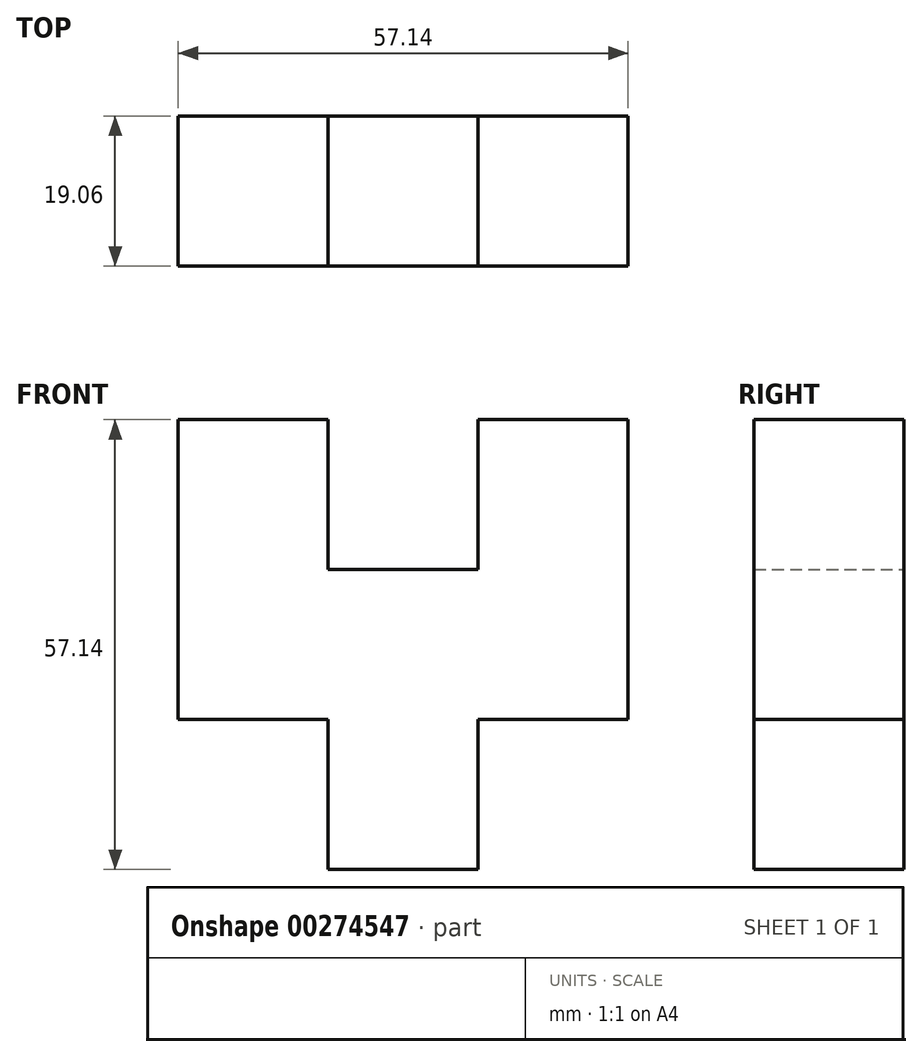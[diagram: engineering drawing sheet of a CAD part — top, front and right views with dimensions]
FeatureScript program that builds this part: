
annotation { "Feature Type Name" : "Feature", "Feature Type Description" : "" }
export const myFeature = defineFeature(function(context is Context, id is Id, definition is map)
    precondition{}
    {
        {
            var Q0;
            Q0=qCreatedBy(makeId("Front.planeOp"),FACE);
            var sketch = newSketch(context, id + "F0", { "sketchPlane" : qUnion([Q0])});
            skLineSegment(sketch, "E0.bottom", {"start": v(-9.53, 9.53) * mm, "end": v(9.53, 9.53) * mm});
            skLineSegment(sketch, "E0.top", {"start": v(-9.53, -9.53) * mm, "end": v(9.53, -9.53) * mm});
            skLineSegment(sketch, "E0.left", {"start": v(-9.53, 9.53) * mm, "end": v(-9.53, -9.53) * mm});
            skLineSegment(sketch, "E0.right", {"start": v(9.53, 9.53) * mm, "end": v(9.53, -9.53) * mm});
            skPoint(sketch, "E0.middle", {"position": v(0, 0) * mm});
            skLineSegment(sketch, "E1.top", {"start": v(9.53, -9.53) * mm, "end": v(28.58, -9.53) * mm});
            skLineSegment(sketch, "E1.right", {"start": v(28.58, 9.53) * mm, "end": v(28.58, -9.53) * mm});
            skPoint(sketch, "E1.middle", {"position": v(19.05, 0) * mm});
            skLineSegment(sketch, "E2.bottom", {"start": v(-28.58, 9.52) * mm, "end": v(-9.53, 9.52) * mm});
            skLineSegment(sketch, "E2.top", {"start": v(-28.58, -9.53) * mm, "end": v(-9.53, -9.53) * mm});
            skLineSegment(sketch, "E2.left", {"start": v(-28.58, 9.52) * mm, "end": v(-28.58, -9.53) * mm});
            skLineSegment(sketch, "E2.right", {"start": v(-9.53, 9.52) * mm, "end": v(-9.53, -9.53) * mm});
            skPoint(sketch, "E2.middle", {"position": v(-19.05, 0) * mm});
            skLineSegment(sketch, "E3.bottom", {"start": v(-28.58, 28.58) * mm, "end": v(-9.53, 28.58) * mm});
            skLineSegment(sketch, "E3.left", {"start": v(-28.58, 28.58) * mm, "end": v(-28.58, 9.52) * mm});
            skLineSegment(sketch, "E3.right", {"start": v(-9.53, 28.58) * mm, "end": v(-9.53, 9.52) * mm});
            skPoint(sketch, "E3.middle", {"position": v(-19.05, 19.05) * mm});
            skLineSegment(sketch, "E4.bottom", {"start": v(9.53, 28.57) * mm, "end": v(28.58, 28.57) * mm});
            skLineSegment(sketch, "E4.top", {"start": v(9.53, 9.52) * mm, "end": v(28.58, 9.52) * mm});
            skLineSegment(sketch, "E4.left", {"start": v(9.53, 28.57) * mm, "end": v(9.53, 9.52) * mm});
            skLineSegment(sketch, "E4.right", {"start": v(28.58, 28.57) * mm, "end": v(28.58, 9.52) * mm});
            skPoint(sketch, "E4.middle", {"position": v(19.05, 19.05) * mm});
            skLineSegment(sketch, "E5.bottom", {"start": v(-9.53, -9.53) * mm, "end": v(9.52, -9.53) * mm});
            skLineSegment(sketch, "E5.top", {"start": v(-9.53, -28.58) * mm, "end": v(9.52, -28.58) * mm});
            skLineSegment(sketch, "E5.left", {"start": v(-9.53, -9.53) * mm, "end": v(-9.53, -28.58) * mm});
            skLineSegment(sketch, "E5.right", {"start": v(9.52, -9.53) * mm, "end": v(9.52, -28.58) * mm});
            skPoint(sketch, "E5.middle", {"position": v(0, -19.05) * mm});
            skLineSegment(sketch, "E6", {"start": v(9.53, 9.53) * mm, "end": v(28.58, 9.53) * mm});
            skSolve(sketch);
        }
        {
            var Q0;
            Q0 = qSketchRegion(id + "F0", true);
            extrude(context, id + "F1", {"entities" : qUnion([Q0]), "endBound" : BoundingType.SYMMETRIC, "depth" : 19.05 * mm});
        }
    });
